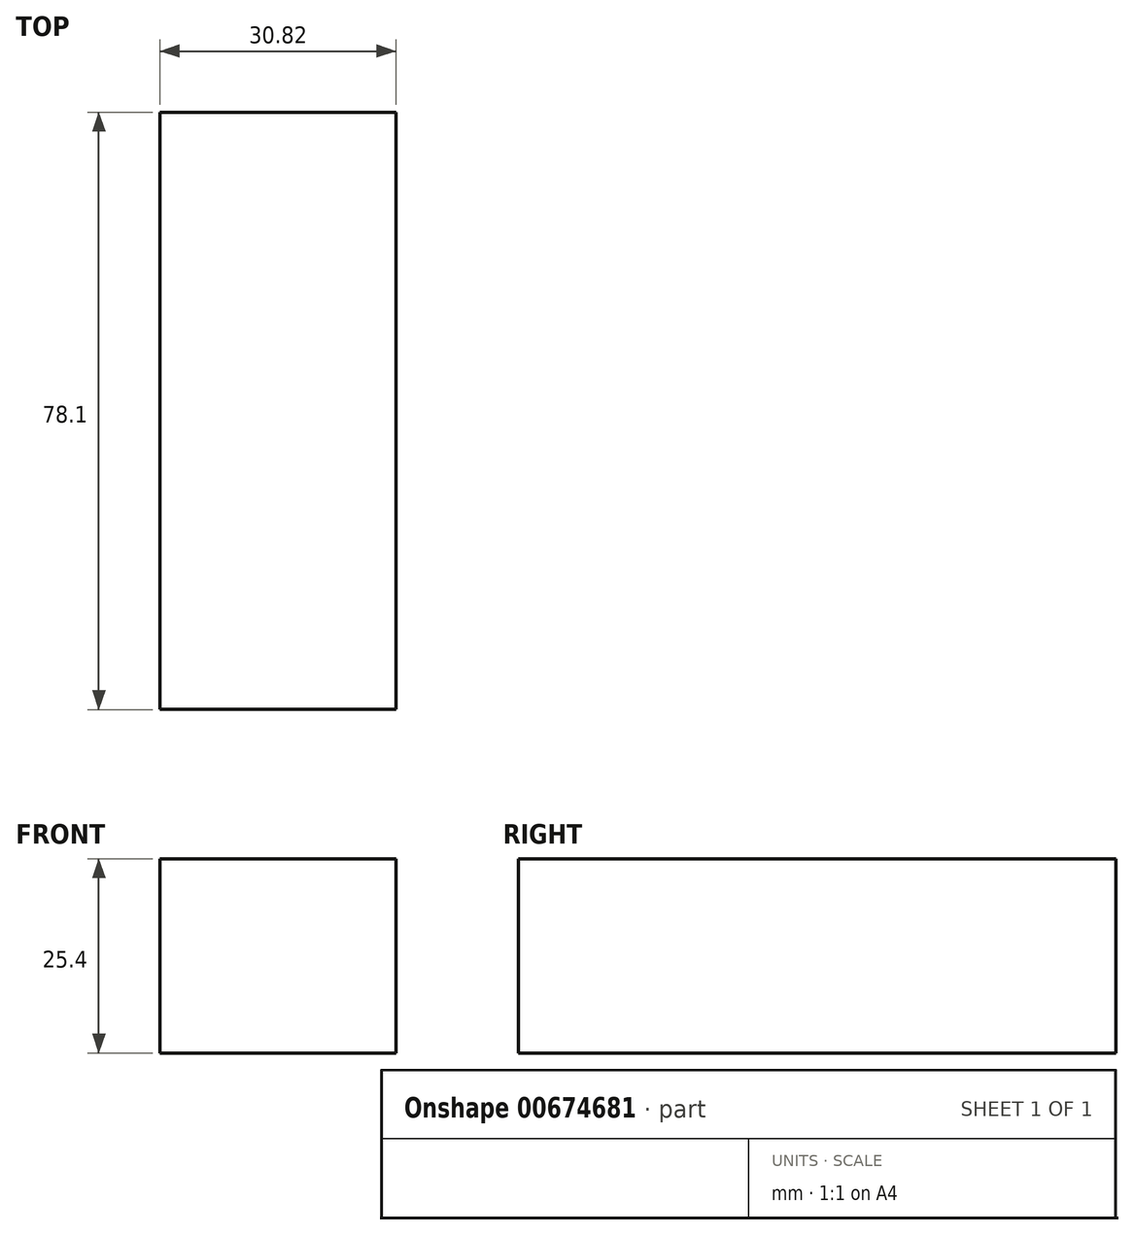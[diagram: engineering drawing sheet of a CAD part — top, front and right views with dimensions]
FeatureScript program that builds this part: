
annotation { "Feature Type Name" : "Feature", "Feature Type Description" : "" }
export const myFeature = defineFeature(function(context is Context, id is Id, definition is map)
    precondition{}
    {
        {
            var Q0;
            Q0=qCreatedBy(makeId("Top.planeOp"),FACE);
            var sketch = newSketch(context, id + "F0", { "sketchPlane" : qUnion([Q0])});
            skLineSegment(sketch, "E0.bottom", {"start": v(53.03, 46.24) * mm, "end": v(22.2, 46.24) * mm});
            skLineSegment(sketch, "E0.top", {"start": v(53.03, -31.86) * mm, "end": v(22.2, -31.86) * mm});
            skLineSegment(sketch, "E0.left", {"start": v(53.03, 46.24) * mm, "end": v(53.03, -31.86) * mm});
            skLineSegment(sketch, "E0.right", {"start": v(22.2, 46.24) * mm, "end": v(22.2, -31.86) * mm});
            skLineSegment(sketch, "E1.bottom", {"start": v(53.03, -31.86) * mm, "end": v(39.32, -31.86) * mm});
            skLineSegment(sketch, "E1.top", {"start": v(53.03, -53.94) * mm, "end": v(39.32, -53.94) * mm});
            skLineSegment(sketch, "E1.left", {"start": v(53.03, -31.86) * mm, "end": v(53.03, -53.94) * mm});
            skLineSegment(sketch, "E1.right", {"start": v(39.32, -31.86) * mm, "end": v(39.32, -53.94) * mm});
            skSolve(sketch);
        }
        {
            var Q0;
            Q0=makeQuery(id+"F0.imprint","IMPRINT",FACE,{"disambiguationData":[TD([[makeQuery(id+"F0.imprint","IMPRINT",EDGE,{"derivedFrom":sQuery(id+"F0.wireOp",EDGE,"E0.bottom")}),1.0]])]});
            extrude(context, id + "F1", {"entities" : qUnion([Q0]), "depth" : 25.4 * mm, "offsetDistance" : 25.4 * mm});
        }
    });
